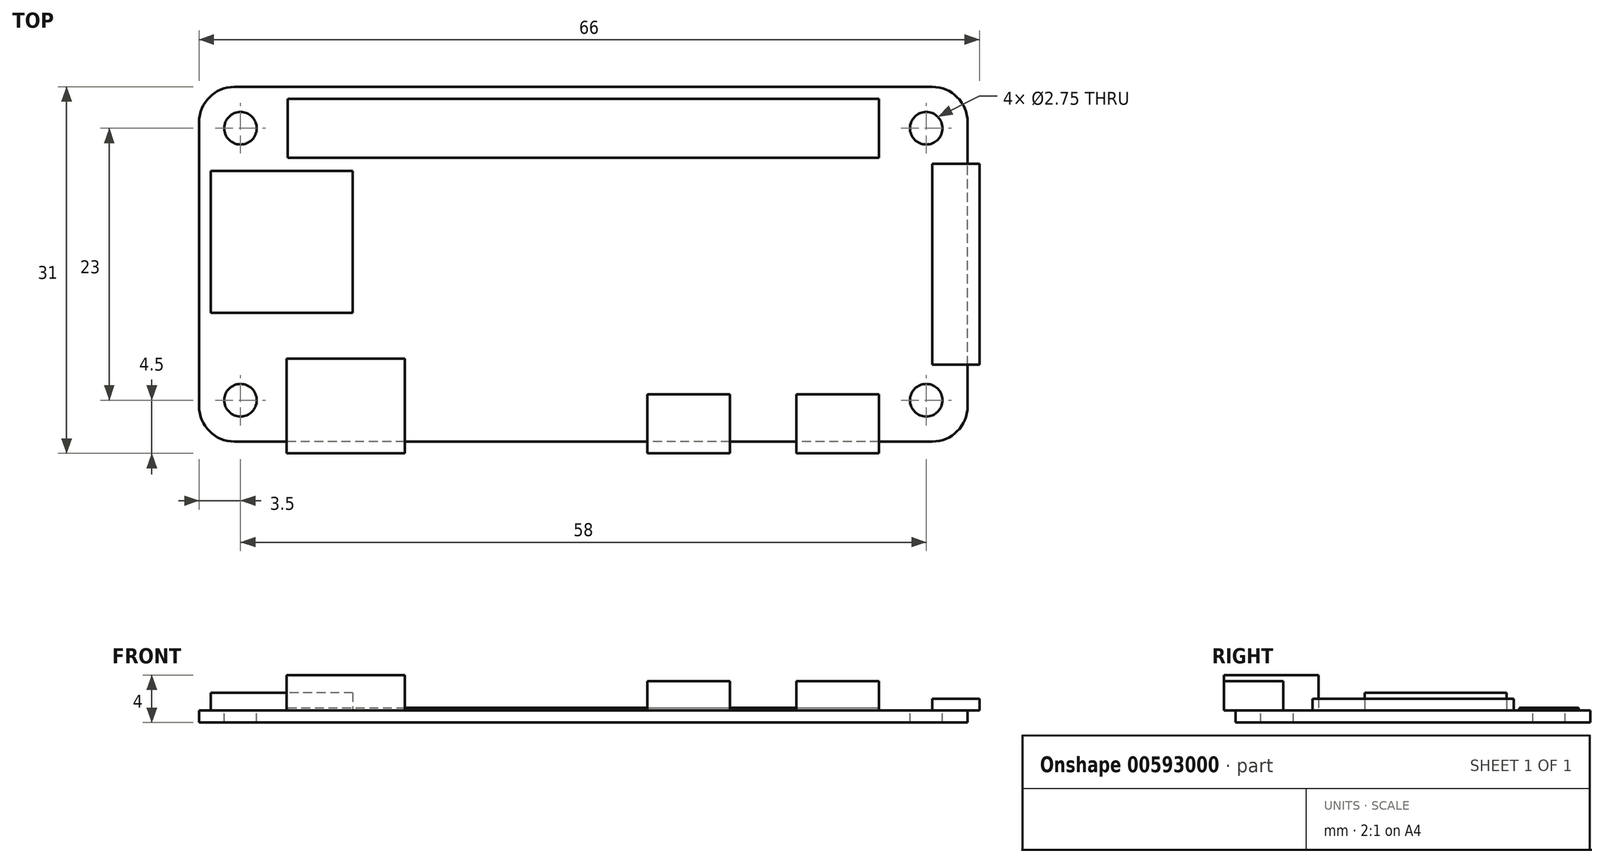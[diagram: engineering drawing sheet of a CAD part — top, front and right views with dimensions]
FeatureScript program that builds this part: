
annotation { "Feature Type Name" : "Feature", "Feature Type Description" : "" }
export const myFeature = defineFeature(function(context is Context, id is Id, definition is map)
    precondition{}
    {
        {
            var Q0;
            Q0=qCreatedBy(makeId("Top.planeOp"),FACE);
            var sketch = newSketch(context, id + "F0", { "sketchPlane" : qUnion([Q0])});
            skLineSegment(sketch, "E0.bottom", {"start": v(29.5, -15) * mm, "end": v(-29.5, -15) * mm});
            skLineSegment(sketch, "E0.top", {"start": v(29.5, 15) * mm, "end": v(-29.5, 15) * mm});
            skLineSegment(sketch, "E0.right", {"start": v(-32.5, -12) * mm, "end": v(-32.5, 12) * mm});
            skPoint(sketch, "E0.middle", {"position": v(0, 0) * mm});
            skPoint(sketch, "E1.visualSharp", {"position": v(-32.5, 15) * mm});
            skArc(sketch, "E1.filletArc", {"start": v(-29.5, 15) * mm, "mid": v(-31.62, 14.12) * mm, "end": v(-32.5, 12) * mm});
            skPoint(sketch, "E2.visualSharp", {"position": v(32.5, 15) * mm});
            skPoint(sketch, "E3.visualSharp", {"position": v(32.5, -15) * mm});
            skPoint(sketch, "E4.visualSharp", {"position": v(-32.5, -15) * mm});
            skArc(sketch, "E4.filletArc", {"start": v(-32.5, -12) * mm, "mid": v(-31.62, -14.12) * mm, "end": v(-29.5, -15) * mm});
            skLineSegment(sketch, "E5.bottom", {"start": v(-19.5, -4.1) * mm, "end": v(-31.5, -4.1) * mm});
            skLineSegment(sketch, "E5.top", {"start": v(-19.5, 7.9) * mm, "end": v(-31.5, 7.9) * mm});
            skLineSegment(sketch, "E5.left", {"start": v(-19.5, -4.1) * mm, "end": v(-19.5, 7.9) * mm});
            skLineSegment(sketch, "E5.right", {"start": v(-31.5, -4.1) * mm, "end": v(-31.5, 7.9) * mm});
            skPoint(sketch, "E5.middle", {"position": v(-25.5, 1.9) * mm});
            skCircle(sketch, "E6", {"center": v(-29, 11.5) * mm, "radius": 1.38 * mm});
            skLineSegment(sketch, "E7", {"start": v(0, 0) * mm, "end": v(0, 6.42) * mm, "construction": true});
            skLineSegment(sketch, "E8", {"start": v(0, 0) * mm, "end": v(-5.84, 0) * mm, "construction": true});
            skCircle(sketch, "E9.MirrorC", {"center": v(29, 11.5) * mm, "radius": 1.38 * mm});
            skCircle(sketch, "E10.MirrorC", {"center": v(-29, -11.5) * mm, "radius": 1.38 * mm});
            skCircle(sketch, "E11.MirrorC", {"center": v(29, -11.5) * mm, "radius": 1.38 * mm});
            skLineSegment(sketch, "E12", {"start": v(-20.1, -15) * mm, "end": v(-20.1, -12) * mm, "construction": true});
            skLineSegment(sketch, "E13", {"start": v(8.9, -15) * mm, "end": v(8.9, -13.5) * mm, "construction": true});
            skLineSegment(sketch, "E14", {"start": v(21.5, -15) * mm, "end": v(21.5, -13.5) * mm, "construction": true});
            skLineSegment(sketch, "E15.bottom", {"start": v(-15.1, -16) * mm, "end": v(-25.1, -16) * mm});
            skLineSegment(sketch, "E15.top", {"start": v(-15.1, -8) * mm, "end": v(-25.1, -8) * mm});
            skLineSegment(sketch, "E15.left", {"start": v(-15.1, -16) * mm, "end": v(-15.1, -8) * mm});
            skLineSegment(sketch, "E15.right", {"start": v(-25.1, -16) * mm, "end": v(-25.1, -8) * mm});
            skPoint(sketch, "E15.middle", {"position": v(-20.1, -12) * mm});
            skLineSegment(sketch, "E16.bottom", {"start": v(5.4, -11) * mm, "end": v(12.4, -11) * mm});
            skLineSegment(sketch, "E16.top", {"start": v(5.4, -16) * mm, "end": v(12.4, -16) * mm});
            skLineSegment(sketch, "E16.left", {"start": v(5.4, -11) * mm, "end": v(5.4, -16) * mm});
            skLineSegment(sketch, "E16.right", {"start": v(12.4, -11) * mm, "end": v(12.4, -16) * mm});
            skPoint(sketch, "E16.middle", {"position": v(8.9, -13.5) * mm});
            skLineSegment(sketch, "E17.bottom", {"start": v(18, -11) * mm, "end": v(25, -11) * mm});
            skLineSegment(sketch, "E17.top", {"start": v(18, -16) * mm, "end": v(25, -16) * mm});
            skLineSegment(sketch, "E17.left", {"start": v(18, -11) * mm, "end": v(18, -16) * mm});
            skLineSegment(sketch, "E17.right", {"start": v(25, -11) * mm, "end": v(25, -16) * mm});
            skPoint(sketch, "E17.middle", {"position": v(21.5, -13.5) * mm});
            skLineSegment(sketch, "E18", {"start": v(-29, 11.5) * mm, "end": v(0, 11.5) * mm, "construction": true});
            skLineSegment(sketch, "E19.bottom", {"start": v(-25, 9) * mm, "end": v(25, 9) * mm});
            skLineSegment(sketch, "E19.top", {"start": v(-25, 14) * mm, "end": v(25, 14) * mm});
            skLineSegment(sketch, "E19.left", {"start": v(-25, 9) * mm, "end": v(-25, 14) * mm});
            skLineSegment(sketch, "E19.right", {"start": v(25, 9) * mm, "end": v(25, 14) * mm});
            skPoint(sketch, "E19.middle", {"position": v(0, 11.5) * mm});
            skLineSegment(sketch, "E20", {"start": v(32.5, -12) * mm, "end": v(32.5, 12) * mm});
            skArc(sketch, "E21.filletArc", {"start": v(32.5, 12) * mm, "mid": v(31.62, 14.12) * mm, "end": v(29.5, 15) * mm});
            skArc(sketch, "E22.filletArc", {"start": v(29.5, -15) * mm, "mid": v(31.62, -14.12) * mm, "end": v(32.5, -12) * mm});
            skLineSegment(sketch, "E23.bottom", {"start": v(33.5, -8.5) * mm, "end": v(29.5, -8.5) * mm});
            skLineSegment(sketch, "E23.top", {"start": v(33.5, 8.5) * mm, "end": v(29.5, 8.5) * mm});
            skLineSegment(sketch, "E23.left", {"start": v(33.5, -8.5) * mm, "end": v(33.5, 8.5) * mm});
            skLineSegment(sketch, "E23.right", {"start": v(29.5, -8.5) * mm, "end": v(29.5, 8.5) * mm});
            skPoint(sketch, "E23.middle", {"position": v(31.5, 0) * mm});
            skSolve(sketch);
        }
        {
            var Q0;
            Q0=makeQuery(id+"F0.imprint","IMPRINT",FACE,{"disambiguationData":[TD([[makeQuery(id+"F0.imprint","IMPRINT",EDGE,{"derivedFrom":sQuery(id+"F0.wireOp",EDGE,"E19.bottom")}),1.0]])]});
            var Q1;
            {var subQ5=sQuery(id+"F0.wireOp",EDGE,"E16.bottom");Q1=makeQuery(id+"F0.imprint","IMPRINT",FACE,{"disambiguationData":[TD([[makeQuery(id+"F0.imprint","IMPRINT",EDGE,{"derivedFrom":subQ5}),-1.0]])]});}
            var Q2;
            Q2=makeQuery(id+"F0.imprint","IMPRINT",FACE,{"disambiguationData":[TD([[makeQuery(id+"F0.imprint","IMPRINT",EDGE,{"derivedFrom":sQuery(id+"F0.wireOp",EDGE,"E5.bottom")}),-1.0]])]});
            var Q3;
            {var subQ5=sQuery(id+"F0.wireOp",EDGE,"E15.top");Q3=makeQuery(id+"F0.imprint","IMPRINT",FACE,{"disambiguationData":[TD([[makeQuery(id+"F0.imprint","IMPRINT",EDGE,{"derivedFrom":subQ5}),1.0]])]});}
            var Q4;
            Q4=makeQuery(id+"F0.imprint","IMPRINT",FACE,{"disambiguationData":[TD([[makeQuery(id+"F0.imprint","IMPRINT",EDGE,{"derivedFrom":sQuery(id+"F0.wireOp",EDGE,"E0.top")}),1.0]])]});
            var Q5;
            {var subQ5=sQuery(id+"F0.wireOp",EDGE,"E17.bottom");Q5=makeQuery(id+"F0.imprint","IMPRINT",FACE,{"disambiguationData":[TD([[makeQuery(id+"F0.imprint","IMPRINT",EDGE,{"derivedFrom":subQ5}),-1.0]])]});}
            var Q6;
            {var subQ5=sQuery(id+"F0.wireOp",EDGE,"E23.right");Q6=makeQuery(id+"F0.imprint","IMPRINT",FACE,{"disambiguationData":[TD([[makeQuery(id+"F0.imprint","IMPRINT",EDGE,{"derivedFrom":subQ5}),-1.0]])]});}
            extrude(context, id + "F1", {"entities" : qUnion([Q0, Q1, Q2, Q3, Q4, Q5, Q6]), "oppositeDirection" : true, "depth" : 1 * mm, "offsetDistance" : 25 * mm});
        }
        {
            var Q0;
            Q0=makeQuery(id+"F0.imprint","IMPRINT",FACE,{"disambiguationData":[TD([[makeQuery(id+"F0.imprint","IMPRINT",EDGE,{"derivedFrom":sQuery(id+"F0.wireOp",EDGE,"E5.bottom")}),-1.0]])]});
            extrude(context, id + "F2", {"entities" : qUnion([Q0]), "depth" : 1.5 * mm, "offsetDistance" : 25 * mm});
        }
        {
            var Q0;
            {var subQ5=sQuery(id+"F0.wireOp",EDGE,"E15.top");Q0=makeQuery(id+"F0.imprint","IMPRINT",FACE,{"disambiguationData":[TD([[makeQuery(id+"F0.imprint","IMPRINT",EDGE,{"derivedFrom":subQ5}),1.0]])]});}
            var Q1;
            {var subQ5=sQuery(id+"F0.wireOp",EDGE,"E15.bottom");Q1=makeQuery(id+"F0.imprint","IMPRINT",FACE,{"disambiguationData":[TD([[makeQuery(id+"F0.imprint","IMPRINT",EDGE,{"derivedFrom":subQ5}),-1.0]])]});}
            extrude(context, id + "F3", {"entities" : qUnion([Q0, Q1]), "operationType" : NewBodyOperationType.ADD, "depth" : 3 * mm, "offsetDistance" : 25 * mm});
        }
        {
            var Q0;
            {var subQ5=sQuery(id+"F0.wireOp",EDGE,"E16.bottom");Q0=makeQuery(id+"F0.imprint","IMPRINT",FACE,{"disambiguationData":[TD([[makeQuery(id+"F0.imprint","IMPRINT",EDGE,{"derivedFrom":subQ5}),-1.0]])]});}
            var Q1;
            {var subQ5=sQuery(id+"F0.wireOp",EDGE,"E16.top");Q1=makeQuery(id+"F0.imprint","IMPRINT",FACE,{"disambiguationData":[TD([[makeQuery(id+"F0.imprint","IMPRINT",EDGE,{"derivedFrom":subQ5}),1.0]])]});}
            var Q2;
            {var subQ5=sQuery(id+"F0.wireOp",EDGE,"E17.bottom");Q2=makeQuery(id+"F0.imprint","IMPRINT",FACE,{"disambiguationData":[TD([[makeQuery(id+"F0.imprint","IMPRINT",EDGE,{"derivedFrom":subQ5}),-1.0]])]});}
            var Q3;
            {var subQ5=sQuery(id+"F0.wireOp",EDGE,"E17.top");Q3=makeQuery(id+"F0.imprint","IMPRINT",FACE,{"disambiguationData":[TD([[makeQuery(id+"F0.imprint","IMPRINT",EDGE,{"derivedFrom":subQ5}),1.0]])]});}
            extrude(context, id + "F4", {"entities" : qUnion([Q0, Q1, Q2, Q3]), "depth" : 2.5 * mm, "offsetDistance" : 25 * mm});
        }
        {
            var Q0;
            {var subQ5=sQuery(id+"F0.wireOp",EDGE,"E23.left");Q0=makeQuery(id+"F0.imprint","IMPRINT",FACE,{"disambiguationData":[TD([[makeQuery(id+"F0.imprint","IMPRINT",EDGE,{"derivedFrom":subQ5}),1.0]])]});}
            var Q1;
            {var subQ5=sQuery(id+"F0.wireOp",EDGE,"E23.right");Q1=makeQuery(id+"F0.imprint","IMPRINT",FACE,{"disambiguationData":[TD([[makeQuery(id+"F0.imprint","IMPRINT",EDGE,{"derivedFrom":subQ5}),-1.0]])]});}
            extrude(context, id + "F5", {"entities" : qUnion([Q0, Q1]), "depth" : 1 * mm, "offsetDistance" : 25 * mm});
        }
        {
            var Q0;
            Q0=makeQuery(id+"F0.imprint","IMPRINT",FACE,{"disambiguationData":[TD([[makeQuery(id+"F0.imprint","IMPRINT",EDGE,{"derivedFrom":sQuery(id+"F0.wireOp",EDGE,"E19.bottom")}),1.0]])]});
            extrude(context, id + "F6", {"entities" : qUnion([Q0]), "depth" : 0.25 * mm, "offsetDistance" : 25 * mm});
        }
    });
